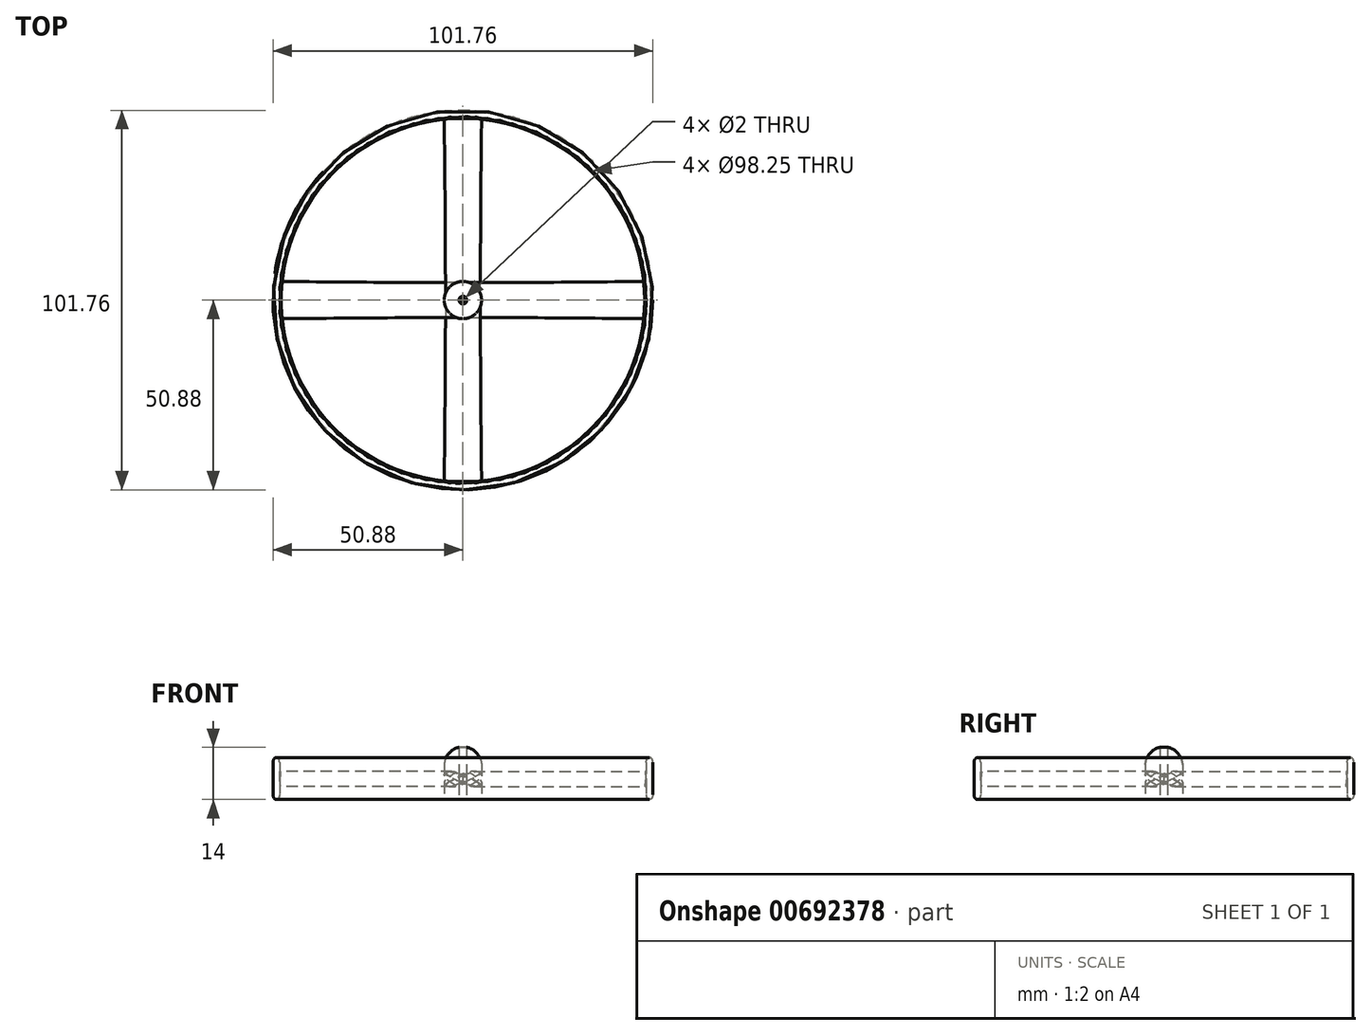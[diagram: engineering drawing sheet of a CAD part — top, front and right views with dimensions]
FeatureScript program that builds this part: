
annotation { "Feature Type Name" : "Feature", "Feature Type Description" : "" }
export const myFeature = defineFeature(function(context is Context, id is Id, definition is map)
    precondition{}
    {
        {
            var Q0;
            Q0=qCreatedBy(makeId("Top.planeOp"),FACE);
            var sketch = newSketch(context, id + "F0", { "sketchPlane" : qUnion([Q0])});
            skCircle(sketch, "E0", {"center": v(0, 0) * mm, "radius": 5 * mm});
            skCircle(sketch, "E1", {"center": v(0, 0) * mm, "radius": 1 * mm});
            skSolve(sketch);
        }
        {
            var Q0;
            Q0=makeQuery(id+"F0.imprint","IMPRINT",FACE,{"disambiguationData":[TD([[makeQuery(id+"F0.imprint","IMPRINT",EDGE,{"derivedFrom":sQuery(id+"F0.wireOp",EDGE,"E0")}),1.0]])]});
            extrude(context, id + "F1", {"entities" : qUnion([Q0]), "depth" : 14 * mm, "offsetDistance" : 25 * mm});
        }
        {
            var Q0;
            Q0=makeQuery(id+"F1.opExtrude","CAP_EDGE",EDGE,{"disambiguationData":[OSD([sQuery(id+"F0.wireOp",EDGE,"E0")])],"isStart":false});
            fillet(context, id + "F2", {"entities" : qUnion([Q0]), "radius" : 4.8 * mm, "tangentPropagation" : true, "rho" : 0.4, "crossSection" : FilletCrossSection.CONIC, "allowEdgeOverflow" : false});
        }
        {
            var Q0;
            Q0=qCreatedBy(makeId("Front.planeOp"),FACE);
            var sketch = newSketch(context, id + "F3", { "sketchPlane" : qUnion([Q0])});
            skLineSegment(sketch, "E2", {"start": v(-5, 8.9) * mm, "end": v(-5, 0) * mm, "construction": true});
            skLineSegment(sketch, "E3", {"start": v(5, 8.9) * mm, "end": v(5, 0) * mm, "construction": true});
            skEllipse(sketch, "E4", {"center": v(0, 5.5) * mm, "majorRadius": 5 * mm, "minorRadius": 0.93 * mm, "majorAxis": v(-0.93, -0.37)});
            skPoint(sketch, "E5", {"position": v(-4.64, 3.64) * mm});
            skPoint(sketch, "E5.positionSnap0", {"position": v(-4.64, 3.64) * mm});
            skLineSegment(sketch, "E6", {"start": v(-5, 0) * mm, "end": v(0, 0) * mm, "construction": true});
            skSolve(sketch);
        }
        {
            var Q0;
            Q0=qCreatedBy(makeId("Front.planeOp"),FACE);
            cPlane(context, id + "F4", {"entities" : qUnion([Q0]), "cplaneType" : CPlaneType.OFFSET, "offset" : 50 * mm, "width" : 150 * mm, "height" : 150 * mm});
        }
        {
            var Q0;
            Q0=qCreatedBy(id+"F4.planeOp",FACE);
            var sketch = newSketch(context, id + "F5", { "sketchPlane" : qUnion([Q0])});
            skLineSegment(sketch, "E7", {"start": v(-5, 8.9) * mm, "end": v(-5, 0) * mm, "construction": true});
            skLineSegment(sketch, "E8", {"start": v(5, 8.9) * mm, "end": v(5, 0) * mm, "construction": true});
            skEllipse(sketch, "E9", {"center": v(0, 5.5) * mm, "majorRadius": 5.35 * mm, "minorRadius": 0.93 * mm, "majorAxis": v(-0.93, -0.36)});
            skPoint(sketch, "E10", {"position": v(-5, 3.6) * mm});
            skPoint(sketch, "E10.positionSnap0", {"position": v(-5, 3.6) * mm});
            skLineSegment(sketch, "E11", {"start": v(-5, 0) * mm, "end": v(0, 0) * mm, "construction": true});
            skSolve(sketch);
        }
        {
            var Q1;
            Q1 = qSketchRegion(id + "F3", true);
            var Q2;
            Q2 = qSketchRegion(id + "F5", true);
            loft(context, id + "F6", {"operationType" : NewBodyOperationType.ADD, "sheetProfilesArray" : [{ "sheetProfileEntities" : qUnion([Q1]) }, { "sheetProfileEntities" : qUnion([Q2]) }]});
        }
        {
            var Q0;
            Q0=qCreatedBy(makeId("Right.planeOp"),FACE);
            var sketch = newSketch(context, id + "F7", { "sketchPlane" : qUnion([Q0])});
            skLineSegment(sketch, "E12", {"start": v(-49.12, 0) * mm, "end": v(-49.12, 11.25) * mm});
            skLineSegment(sketch, "E13", {"start": v(-49.13, 11.25) * mm, "end": v(-50.88, 11.25) * mm, "construction": true});
            skLineSegment(sketch, "E14", {"start": v(-50.88, 11.25) * mm, "end": v(-50.88, 0) * mm});
            skLineSegment(sketch, "E15", {"start": v(-50.88, 0) * mm, "end": v(-49.12, 0) * mm, "construction": true});
            skPoint(sketch, "E16", {"position": v(-50, 0) * mm});
            skPoint(sketch, "E17", {"position": v(-50, 11.25) * mm});
            skPoint(sketch, "E18", {"position": v(-50, 9.95) * mm});
            skPoint(sketch, "E19", {"position": v(-50, 1.3) * mm});
            skPoint(sketch, "E20", {"position": v(-49.12, 9.95) * mm});
            skPoint(sketch, "E21", {"position": v(-49.12, 1.3) * mm});
            skEllipse(sketch, "E22", {"center": v(-50, 1.3) * mm, "majorRadius": 1.3 * mm, "minorRadius": 0.88 * mm, "majorAxis": v(0, -1)});
            skEllipse(sketch, "E23", {"center": v(-50, 9.95) * mm, "majorRadius": 0.88 * mm, "minorRadius": 1.3 * mm, "majorAxis": v(1, 0)});
            skLineSegment(sketch, "E24", {"start": v(0, 0) * mm, "end": v(0, 24.8) * mm, "construction": true});
            skSolve(sketch);
        }
        {
            var Q0;
            {var subQ0=sQuery(id+"F7.wireOp",EDGE,"E23");var subQ1=makeQuery(id+"F7.imprint","INTERSECT",VERTEX,{"derivedFrom":[sQuery(id+"F7.wireOp",EDGE,"E12"),subQ0]});Q0=makeQuery(id+"F7.imprint","IMPRINT",FACE,{"disambiguationData":[TD([[makeQuery(id+"F7.imprint","IMPRINT",EDGE,{"disambiguationData":[TD([[subQ1,1.0]])],"derivedFrom":subQ0}),1.0]])]});}
            var Q1;
            {var subQ0=sQuery(id+"F7.wireOp",EDGE,"E22");var subQ1=sQuery(id+"F7.wireOp",EDGE,"E12");var subQ2=makeQuery(id+"F7.imprint","INTERSECT",VERTEX,{"derivedFrom":[subQ1,subQ0]});Q1=makeQuery(id+"F7.imprint","IMPRINT",FACE,{"disambiguationData":[TD([[makeQuery(id+"F7.imprint","IMPRINT",EDGE,{"disambiguationData":[TD([[subQ2,-1.0]])],"derivedFrom":subQ1}),1.0]])]});}
            var Q2;
            {var subQ0=sQuery(id+"F7.wireOp",EDGE,"E22");var subQ1=makeQuery(id+"F7.imprint","INTERSECT",VERTEX,{"derivedFrom":[sQuery(id+"F7.wireOp",EDGE,"E12"),subQ0]});Q2=makeQuery(id+"F7.imprint","IMPRINT",FACE,{"disambiguationData":[TD([[makeQuery(id+"F7.imprint","IMPRINT",EDGE,{"disambiguationData":[TD([[subQ1,-1.0]])],"derivedFrom":subQ0}),1.0]])]});}
            var Q3;
            Q3=sQuery(id+"F7.wireOp",EDGE,"E24");
            revolve(context, id + "F8", {"operationType" : NewBodyOperationType.ADD, "entities" : qUnion([Q0, Q1, Q2]), "axis" : qUnion([Q3]), "revolveType" : RevolveType.FULL});
        }
        {
            var Q0;
            Q0=makeQuery(id+"F1.opExtrude","SWEPT_BODY",BODY,{"disambiguationData":[OSD([sQuery(id+"F0.wireOp",EDGE,"E0"),sQuery(id+"F0.wireOp",EDGE,"E1")])]});
            var Q1;
            Q1=sQuery(id+"F7.wireOp",EDGE,"E24");
            circularPattern(context, id + "F9", {"entities" : qUnion([Q0]), "axis" : qUnion([Q1]), "angle" : 360 * degree, "instanceCount" : 4, "equalSpace" : true});
        }
    });
